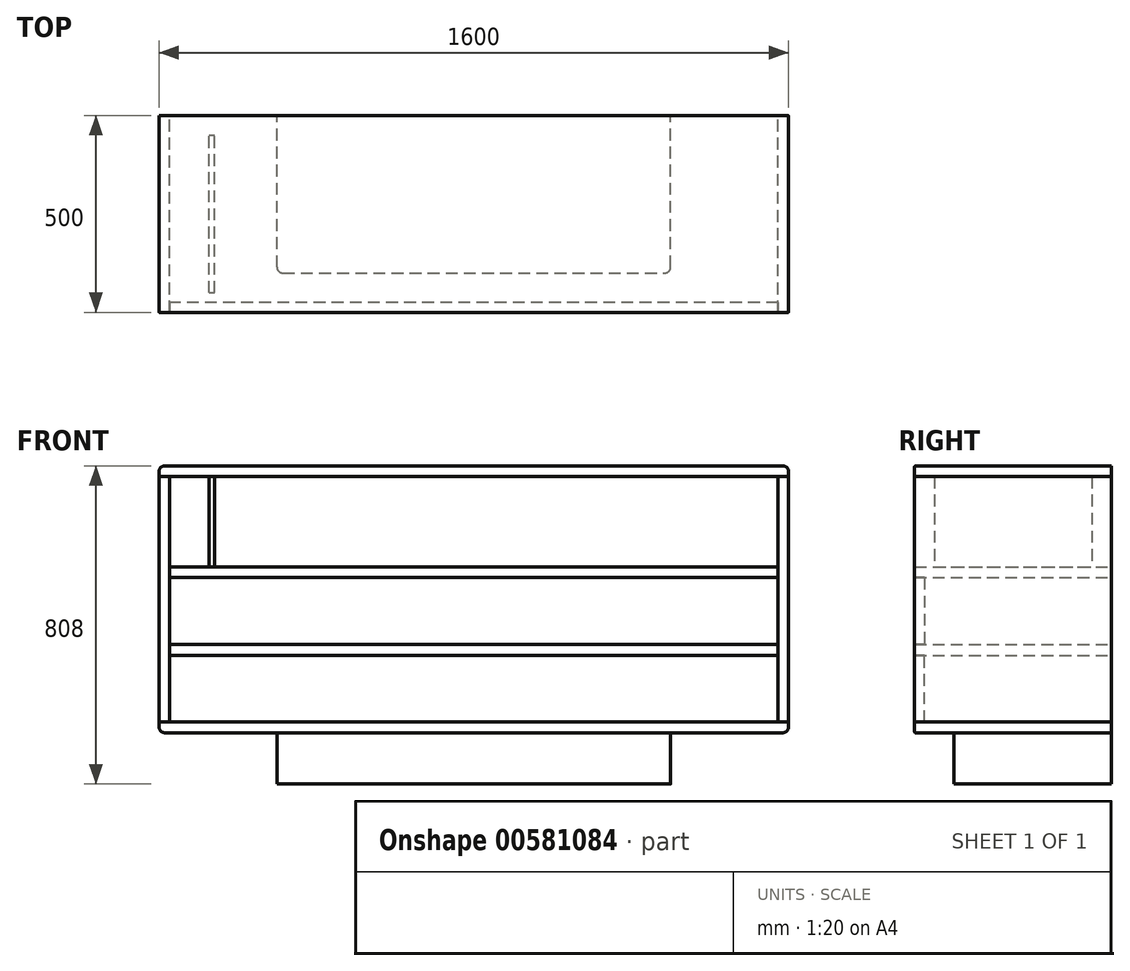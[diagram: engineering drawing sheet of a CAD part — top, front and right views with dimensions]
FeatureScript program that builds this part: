
annotation { "Feature Type Name" : "Feature", "Feature Type Description" : "" }
export const myFeature = defineFeature(function(context is Context, id is Id, definition is map)
    precondition{}
    {
        {
            var Q0;
            Q0=qCreatedBy(makeId("Front.planeOp"),FACE);
            cPlane(context, id + "F0", {"entities" : qUnion([Q0]), "cplaneType" : CPlaneType.OFFSET, "offset" : 500 * mm, "width" : 150 * mm, "height" : 150 * mm});
        }
        {
            var Q0;
            Q0=qCreatedBy(makeId("Right.planeOp"),FACE);
            cPlane(context, id + "F1", {"entities" : qUnion([Q0]), "cplaneType" : CPlaneType.OFFSET, "offset" : 800 * mm, "oppositeDirection" : true, "width" : 150 * mm, "height" : 150 * mm});
        }
        {
            var Q0;
            Q0=qCreatedBy(id+"F1.planeOp",FACE);
            cPlane(context, id + "F2", {"entities" : qUnion([Q0]), "cplaneType" : CPlaneType.OFFSET, "offset" : 27 * mm, "width" : 150 * mm, "height" : 150 * mm});
        }
        {
            var Q0;
            Q0=qCreatedBy(makeId("Top.planeOp"),FACE);
            cPlane(context, id + "F3", {"entities" : qUnion([Q0]), "cplaneType" : CPlaneType.OFFSET, "offset" : 170 * mm, "width" : 150 * mm, "height" : 150 * mm});
        }
        {
            var Q0;
            Q0=qCreatedBy(id+"F3.planeOp",FACE);
            cPlane(context, id + "F4", {"entities" : qUnion([Q0]), "cplaneType" : CPlaneType.OFFSET, "offset" : 27 * mm, "width" : 150 * mm, "height" : 150 * mm});
        }
        {
            var Q0;
            Q0=qCreatedBy(id+"F4.planeOp",FACE);
            cPlane(context, id + "F5", {"entities" : qUnion([Q0]), "cplaneType" : CPlaneType.OFFSET, "offset" : 170 * mm, "width" : 150 * mm, "height" : 150 * mm});
        }
        {
            var Q0;
            Q0=qCreatedBy(id+"F5.planeOp",FACE);
            cPlane(context, id + "F6", {"entities" : qUnion([Q0]), "cplaneType" : CPlaneType.OFFSET, "offset" : 27 * mm, "width" : 150 * mm, "height" : 150 * mm});
        }
        {
            var Q0;
            Q0=qCreatedBy(id+"F6.planeOp",FACE);
            cPlane(context, id + "F7", {"entities" : qUnion([Q0]), "cplaneType" : CPlaneType.OFFSET, "offset" : 230 * mm, "width" : 150 * mm, "height" : 150 * mm});
        }
        {
            var Q0;
            Q0=qCreatedBy(makeId("Front.planeOp"),FACE);
            var sketch = newSketch(context, id + "F8", { "sketchPlane" : qUnion([Q0])});
            skLineSegment(sketch, "E0.bottom", {"start": v(-800, 651) * mm, "end": v(0, 651) * mm});
            skLineSegment(sketch, "E0.top", {"start": v(-800, 624) * mm, "end": v(0, 624) * mm});
            skLineSegment(sketch, "E0.left", {"start": v(-800, 651) * mm, "end": v(-800, 624) * mm});
            skLineSegment(sketch, "E1.MirrorCS", {"start": v(800, 651) * mm, "end": v(0, 651) * mm});
            skLineSegment(sketch, "E2.MirrorCS", {"start": v(800, 651) * mm, "end": v(800, 624) * mm});
            skLineSegment(sketch, "E3.MirrorCS", {"start": v(800, 624) * mm, "end": v(0, 624) * mm});
            skSolve(sketch);
        }
        {
            var Q0;
            Q0=qCreatedBy(makeId("Front.planeOp"),FACE);
            var sketch = newSketch(context, id + "F9", { "sketchPlane" : qUnion([Q0])});
            skLineSegment(sketch, "E4.bottom", {"start": v(-773, 367) * mm, "end": v(0, 367) * mm});
            skLineSegment(sketch, "E4.top", {"start": v(-773, 394) * mm, "end": v(0, 394) * mm});
            skLineSegment(sketch, "E4.left", {"start": v(-773, 367) * mm, "end": v(-773, 394) * mm});
            skLineSegment(sketch, "E5.MirrorCS", {"start": v(773, 367) * mm, "end": v(0, 367) * mm});
            skLineSegment(sketch, "E6.MirrorCS", {"start": v(773, 394) * mm, "end": v(0, 394) * mm});
            skLineSegment(sketch, "E7.MirrorCS", {"start": v(773, 367) * mm, "end": v(773, 394) * mm});
            skSolve(sketch);
        }
        {
            var Q0;
            Q0=qCreatedBy(makeId("Front.planeOp"),FACE);
            var sketch = newSketch(context, id + "F10", { "sketchPlane" : qUnion([Q0])});
            skLineSegment(sketch, "E8.bottom", {"start": v(-773, 170) * mm, "end": v(0, 170) * mm});
            skLineSegment(sketch, "E8.top", {"start": v(-773, 197) * mm, "end": v(0, 197) * mm});
            skLineSegment(sketch, "E8.left", {"start": v(-773, 170) * mm, "end": v(-773, 197) * mm});
            skLineSegment(sketch, "E8.right", {"start": v(0, 170) * mm, "end": v(0, 197) * mm});
            skLineSegment(sketch, "E9.MirrorCS", {"start": v(773, 170) * mm, "end": v(0, 170) * mm});
            skLineSegment(sketch, "E10.MirrorCS", {"start": v(773, 197) * mm, "end": v(0, 197) * mm});
            skLineSegment(sketch, "E11.MirrorCS", {"start": v(773, 170) * mm, "end": v(773, 197) * mm});
            skSolve(sketch);
        }
        {
            var Q0;
            Q0=qCreatedBy(makeId("Front.planeOp"),FACE);
            var sketch = newSketch(context, id + "F11", { "sketchPlane" : qUnion([Q0])});
            skLineSegment(sketch, "E12.bottom", {"start": v(-800, -27) * mm, "end": v(0, -27) * mm});
            skLineSegment(sketch, "E12.top", {"start": v(-800, 0) * mm, "end": v(0, 0) * mm});
            skLineSegment(sketch, "E12.left", {"start": v(-800, 0) * mm, "end": v(-800, -27) * mm});
            skLineSegment(sketch, "E12.right", {"start": v(0, 0) * mm, "end": v(0, -27) * mm});
            skLineSegment(sketch, "E13.MirrorCS", {"start": v(800, -27) * mm, "end": v(0, -27) * mm});
            skLineSegment(sketch, "E14.MirrorCS", {"start": v(800, 0) * mm, "end": v(0, 0) * mm});
            skLineSegment(sketch, "E15.MirrorCS", {"start": v(800, 0) * mm, "end": v(800, -27) * mm});
            skSolve(sketch);
        }
        {
            var Q0;
            Q0=qCreatedBy(makeId("Front.planeOp"),FACE);
            var sketch = newSketch(context, id + "F12", { "sketchPlane" : qUnion([Q0])});
            skLineSegment(sketch, "E16.bottom", {"start": v(-800, 624) * mm, "end": v(-773, 624) * mm});
            skLineSegment(sketch, "E16.top", {"start": v(-800, 0) * mm, "end": v(-773, 0) * mm});
            skLineSegment(sketch, "E16.left", {"start": v(-800, 624) * mm, "end": v(-800, 0) * mm});
            skLineSegment(sketch, "E16.right", {"start": v(-773, 624) * mm, "end": v(-773, 0) * mm});
            skSolve(sketch);
        }
        {
            var Q0;
            Q0 = qSketchRegion(id + "F8", true);
            var Q1;
            Q1 = qSketchRegion(id + "F9", true);
            var Q2;
            Q2 = qSketchRegion(id + "F10", true);
            var Q3;
            Q3 = qSketchRegion(id + "F11", true);
            var Q4;
            Q4 = qSketchRegion(id + "F12", true);
            var Q5;
            Q5=qCreatedBy(id+"F0.planeOp",FACE);
            extrude(context, id + "F13", {"entities" : qUnion([Q0, Q1, Q2, Q3, Q4]), "endBound" : BoundingType.UP_TO_SURFACE, "depth" : 500 * mm, "endBoundEntityFace" : qUnion([Q5]), "offsetDistance" : 25 * mm});
        }
        {
            var Q0;
            Q0=makeQuery(id+"F13.opExtrude","SWEPT_BODY",BODY,{"disambiguationData":[OSD([sQuery(id+"F12.wireOp",EDGE,"E16.bottom"),sQuery(id+"F12.wireOp",EDGE,"E16.top"),sQuery(id+"F12.wireOp",EDGE,"E16.left"),sQuery(id+"F12.wireOp",EDGE,"E16.right")])]});
            var Q1;
            Q1=qCreatedBy(makeId("Right.planeOp"),FACE);
            mirror(context, id + "F14", {"entities" : qUnion([Q0]), "mirrorPlane" : qUnion([Q1])});
        }
        {
            var Q0;
            Q0=qCreatedBy(id+"F0.planeOp",FACE);
            var sketch = newSketch(context, id + "F15", { "sketchPlane" : qUnion([Q0])});
            skLineSegment(sketch, "E17.bottom", {"start": v(773, 367) * mm, "end": v(-773, 367) * mm});
            skLineSegment(sketch, "E17.top", {"start": v(773, 197) * mm, "end": v(-773, 197) * mm});
            skLineSegment(sketch, "E17.left", {"start": v(773, 367) * mm, "end": v(773, 197) * mm});
            skLineSegment(sketch, "E17.right", {"start": v(-773, 367) * mm, "end": v(-773, 197) * mm});
            skPoint(sketch, "E17.middle", {"position": v(0, 282) * mm});
            skLineSegment(sketch, "E18.bottom", {"start": v(773, 0) * mm, "end": v(-773, 0) * mm});
            skLineSegment(sketch, "E18.top", {"start": v(773, 170) * mm, "end": v(-773, 170) * mm});
            skLineSegment(sketch, "E18.left", {"start": v(773, 0) * mm, "end": v(773, 170) * mm});
            skLineSegment(sketch, "E18.right", {"start": v(-773, 0) * mm, "end": v(-773, 170) * mm});
            skPoint(sketch, "E18.middle", {"position": v(0, 85) * mm});
            skSolve(sketch);
        }
        {
            var Q0;
            Q0 = qSketchRegion(id + "F15", true);
            var Q1;
            Q1=qCreatedBy(id+"F0.planeOp",FACE);
            extrude(context, id + "F16", {"entities" : qUnion([Q0]), "oppositeDirection" : true, "depth" : 25 * mm, "endBoundEntityFace" : qUnion([Q1]), "offsetDistance" : 25 * mm});
        }
        {
            var Q0;
            Q0=makeQuery(id+"F13.opExtrude","SWEPT_EDGE",EDGE,{"disambiguationData":[OSD([sQuery(id+"F11.wireOp",EDGE,"E12.bottom"),sQuery(id+"F11.wireOp",EDGE,"E12.left")])]});
            var Q1;
            Q1=makeQuery(id+"F13.opExtrude","SWEPT_EDGE",EDGE,{"disambiguationData":[OSD([sQuery(id+"F8.wireOp",EDGE,"E0.bottom"),sQuery(id+"F8.wireOp",EDGE,"E0.left")])]});
            var Q2;
            Q2=makeQuery(id+"F13.opExtrude","SWEPT_EDGE",EDGE,{"disambiguationData":[OSD([sQuery(id+"F8.wireOp",EDGE,"E1.MirrorCS"),sQuery(id+"F8.wireOp",EDGE,"E2.MirrorCS")])]});
            var Q3;
            Q3=makeQuery(id+"F13.opExtrude","SWEPT_EDGE",EDGE,{"disambiguationData":[OSD([sQuery(id+"F11.wireOp",EDGE,"E13.MirrorCS"),sQuery(id+"F11.wireOp",EDGE,"E15.MirrorCS")])]});
            fillet(context, id + "F17", {"entities" : qUnion([Q0, Q1, Q2, Q3]), "radius" : 15 * mm, "tangentPropagation" : true, "allowEdgeOverflow" : false});
        }
        {
            var Q0;
            Q0=makeQuery(id+"F13.opExtrude","CAP_EDGE",EDGE,{"disambiguationData":[OSD([sQuery(id+"F8.wireOp",EDGE,"E0.bottom"),sQuery(id+"F8.wireOp",EDGE,"E1.MirrorCS")])],"isStart":false});
            var Q1;
            Q1=makeQuery(id+"F13.opExtrude","CAP_EDGE",EDGE,{"disambiguationData":[OSD([sQuery(id+"F12.wireOp",EDGE,"E16.left")])],"isStart":false});
            var Q2;
            Q2=makeQuery(id+"F13.opExtrude","CAP_EDGE",EDGE,{"disambiguationData":[OSD([sQuery(id+"F11.wireOp",EDGE,"E12.bottom"),sQuery(id+"F11.wireOp",EDGE,"E13.MirrorCS")])],"isStart":false});
            var Q3;
            Q3=makeQuery(id+"F14.opPattern","COPY",EDGE,{"derivedFrom":makeQuery(id+"F13.opExtrude","CAP_EDGE",EDGE,{"disambiguationData":[OSD([sQuery(id+"F12.wireOp",EDGE,"E16.left")])],"isStart":false}),"instanceName":"1"});
            fillet(context, id + "F18", {"entities" : qUnion([Q0, Q1, Q2, Q3]), "radius" : 2 * mm, "tangentPropagation" : true, "allowEdgeOverflow" : false});
        }
        {
            var Q0;
            Q0=qCreatedBy(makeId("Front.planeOp"),FACE);
            var sketch = newSketch(context, id + "F19", { "sketchPlane" : qUnion([Q0])});
            skLineSegment(sketch, "E19.bottom", {"start": v(-500, -27) * mm, "end": v(500, -27) * mm});
            skLineSegment(sketch, "E19.top", {"start": v(-500, -157) * mm, "end": v(500, -157) * mm});
            skLineSegment(sketch, "E19.left", {"start": v(-500, -27) * mm, "end": v(-500, -157) * mm});
            skLineSegment(sketch, "E19.right", {"start": v(500, -27) * mm, "end": v(500, -157) * mm});
            skSolve(sketch);
        }
        {
            var Q0;
            Q0 = qSketchRegion(id + "F19", true);
            extrude(context, id + "F20", {"entities" : qUnion([Q0]), "operationType" : NewBodyOperationType.ADD, "depth" : 400 * mm, "offsetDistance" : 25 * mm});
        }
        {
            var Q0;
            Q0=qCreatedBy(makeId("Front.planeOp"),FACE);
            var sketch = newSketch(context, id + "F21", { "sketchPlane" : qUnion([Q0])});
            skLineSegment(sketch, "E20.bottom", {"start": v(-673, 624) * mm, "end": v(-658, 624) * mm});
            skLineSegment(sketch, "E20.top", {"start": v(-673, 394) * mm, "end": v(-658, 394) * mm});
            skLineSegment(sketch, "E20.left", {"start": v(-673, 624) * mm, "end": v(-673, 394) * mm});
            skLineSegment(sketch, "E20.right", {"start": v(-658, 624) * mm, "end": v(-658, 394) * mm});
            skSolve(sketch);
        }
        {
            var Q0;
            Q0 = qSketchRegion(id + "F21", true);
            extrude(context, id + "F22", {"entities" : qUnion([Q0]), "depth" : 450 * mm, "offsetDistance" : 25 * mm, "hasSecondDirection" : true, "secondDirectionOppositeDirection" : true, "secondDirectionDepth" : -50 * mm});
        }
        {
            var Q0;
            Q0=makeQuery(id+"F20.opExtrude","CAP_EDGE",EDGE,{"disambiguationData":[OSD([sQuery(id+"F19.wireOp",EDGE,"E19.left")])],"isStart":false});
            var Q1;
            Q1=makeQuery(id+"F20.opExtrude","CAP_EDGE",EDGE,{"disambiguationData":[OSD([sQuery(id+"F19.wireOp",EDGE,"E19.right")])],"isStart":false});
            fillet(context, id + "F23", {"entities" : qUnion([Q0, Q1]), "radius" : 15 * mm, "tangentPropagation" : true, "allowEdgeOverflow" : false});
        }
    });
